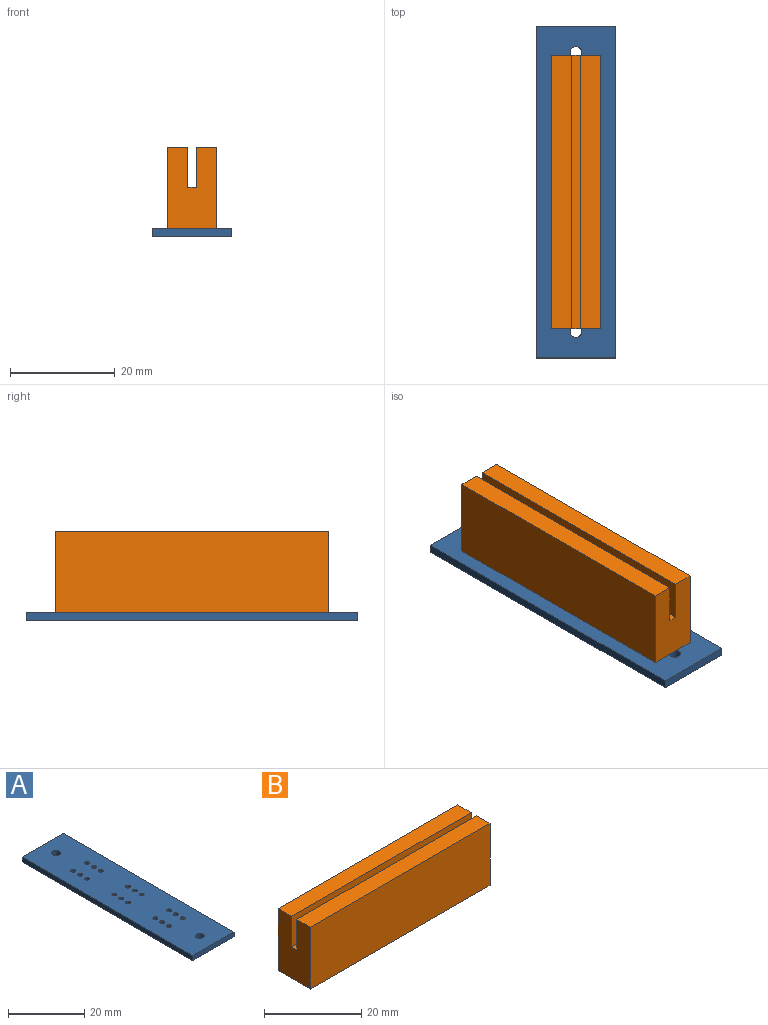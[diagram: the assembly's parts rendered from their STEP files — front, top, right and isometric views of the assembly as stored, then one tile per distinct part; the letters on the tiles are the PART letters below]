
ASSEMBLY  parts=2 mates=1
PART A: 26 faces, bbox 15.2x63.5x1.6 mm
  f0: plane 15.24x1.6mm, normal (0,-1,0), area 24.4mm2, adj f1,f23,f24,f25
  f1: plane 63.5x1.6mm, normal (1,0,0), area 101.6mm2, adj f0,f2,f24,f25
  f2: plane 15.24x1.6mm, normal (0,1,0), area 24.4mm2, adj f1,f23,f24,f25
  f3: cylinder r=1.14mm len=2.29mm, axis (0,0,-1), area 11.5mm2, adj f24,f25
  f4: cylinder r=1.14mm len=2.29mm, axis (0,0,-1), area 11.5mm2, adj f24,f25
  f5: cylinder r=0.64mm len=1.6mm, axis (0,0,-1), area 6.4mm2, adj f24,f25
  f6: cylinder r=0.64mm len=1.6mm, axis (0,0,-1), area 6.4mm2, adj f24,f25
  f7: cylinder r=0.64mm len=1.6mm, axis (0,0,-1), area 6.4mm2, adj f24,f25
  f8: cylinder r=0.64mm len=1.6mm, axis (0,0,-1), area 6.4mm2, adj f24,f25
  f9: cylinder r=0.64mm len=1.6mm, axis (0,0,-1), area 6.4mm2, adj f24,f25
  f10: cylinder r=0.64mm len=1.6mm, axis (0,0,-1), area 6.4mm2, adj f24,f25
  f11: cylinder r=0.64mm len=1.6mm, axis (0,0,-1), area 6.4mm2, adj f24,f25
  f12: cylinder r=0.64mm len=1.6mm, axis (0,0,-1), area 6.4mm2, adj f24,f25
  f13: cylinder r=0.64mm len=1.6mm, axis (0,0,-1), area 6.4mm2, adj f24,f25
  f14: cylinder r=0.64mm len=1.6mm, axis (0,0,-1), area 6.4mm2, adj f24,f25
  f15: cylinder r=0.64mm len=1.6mm, axis (0,0,-1), area 6.4mm2, adj f24,f25
  f16: cylinder r=0.64mm len=1.6mm, axis (0,0,-1), area 6.4mm2, adj f24,f25
  f17: cylinder r=0.64mm len=1.6mm, axis (0,0,-1), area 6.4mm2, adj f24,f25
  f18: cylinder r=0.64mm len=1.6mm, axis (0,0,-1), area 6.4mm2, adj f24,f25
  f19: cylinder r=0.64mm len=1.6mm, axis (0,0,-1), area 6.4mm2, adj f24,f25
  f20: cylinder r=0.64mm len=1.6mm, axis (0,0,-1), area 6.4mm2, adj f24,f25
  f21: cylinder r=0.64mm len=1.6mm, axis (0,0,-1), area 6.4mm2, adj f24,f25
  f22: cylinder r=0.64mm len=1.6mm, axis (0,0,-1), area 6.4mm2, adj f24,f25
  f23: plane 63.5x1.6mm, normal (-1,0,0), area 101.6mm2, adj f0,f2,f24,f25
  f24: plane 63.5x15.24mm, normal (0,0,1), area 936.7mm2, adj f0,f1,f2,f3,f4,f5,f6,f7
  f25: plane 63.5x15.24mm, normal (0,0,-1), area 936.7mm2, adj f0,f1,f2,f3,f4,f5,f6,f7
PART B: 10 faces, bbox 52.3x9.4x15.6 mm
  f0: plane 52.32x3.92mm, normal (0,0,1), area 205.3mm2, adj f1,f2,f3,f7
  f1: plane 15.6x9.4mm, normal (1,0,0), area 134.7mm2, adj f0,f2,f4,f5,f6,f7,f8,f9
  f2: plane 52.32x15.6mm, normal (0,1,0), area 816.3mm2, adj f0,f1,f3,f6
  f3: plane 15.6x9.4mm, normal (-1,0,0), area 134.7mm2, adj f0,f2,f4,f5,f6,f7,f8,f9
  f4: plane 52.32x15.6mm, normal (0,-1,0), area 816.3mm2, adj f1,f3,f5,f6
  f5: plane 52.32x3.92mm, normal (0,0,1), area 205.3mm2, adj f1,f3,f4,f8
  f6: plane 52.32x9.4mm, normal (0,0,-1), area 491.7mm2, adj f1,f2,f3,f4
  f7: plane 52.32x7.7mm, normal (0,-1,0), area 402.9mm2, adj f0,f1,f3,f9
  f8: plane 52.32x7.7mm, normal (0,1,0), area 402.9mm2, adj f1,f3,f5,f9
  f9: plane 52.32x1.55mm, normal (0,0,1), area 81.1mm2, adj f1,f3,f7,f8
PLACE A rot(axis=(1,0,0),180deg) t=(-59.6,13.63,3.19)mm
PLACE B rot(axis=(0,0,1),90deg) t=(-62.52,8.05,3.19)mm
MATE fastened A.f25 <-> B.f6  axis (0,0,1) through (-67.22,-18.12,3.19)mm
